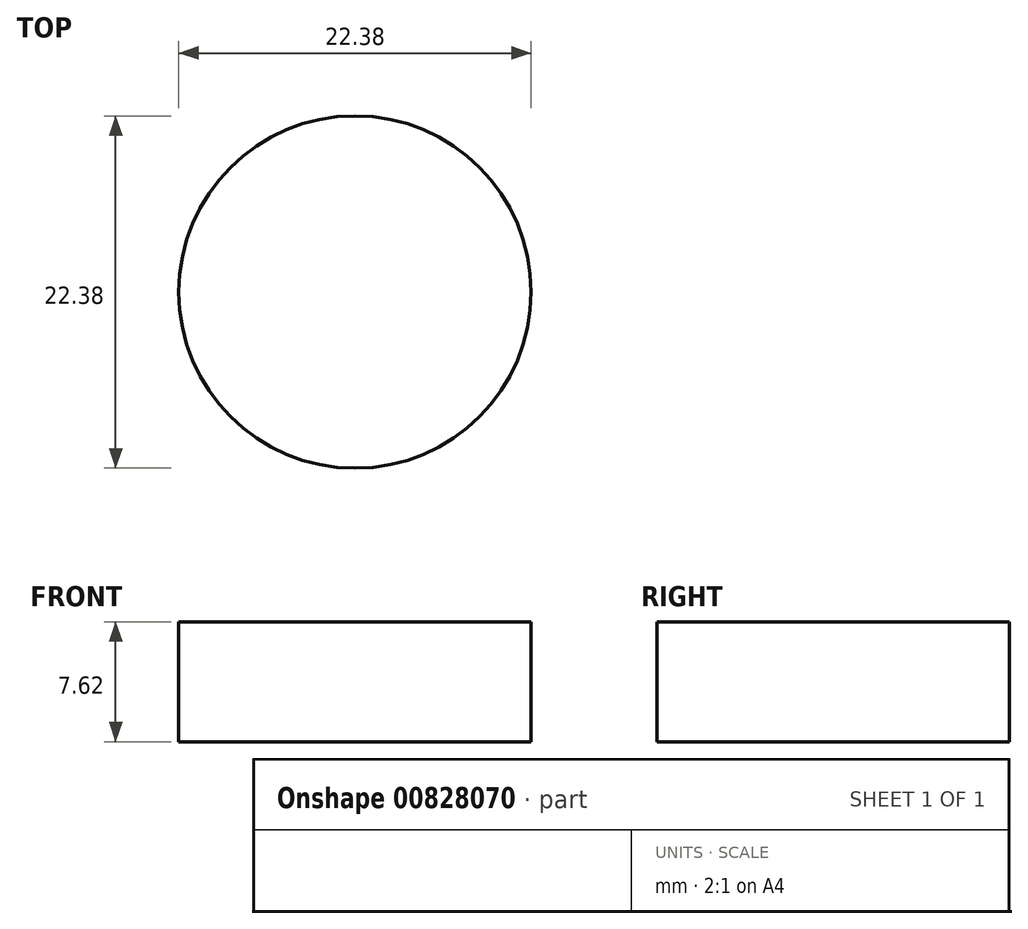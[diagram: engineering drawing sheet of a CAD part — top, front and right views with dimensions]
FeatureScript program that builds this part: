
annotation { "Feature Type Name" : "Feature", "Feature Type Description" : "" }
export const myFeature = defineFeature(function(context is Context, id is Id, definition is map)
    precondition{}
    {
        {
            var Q0;
            Q0=qCreatedBy(makeId("Top.planeOp"),FACE);
            var sketch = newSketch(context, id + "F0", { "sketchPlane" : qUnion([Q0])});
            skCircle(sketch, "E0", {"center": v(0, 0) * mm, "radius": 11.19 * mm});
            skSolve(sketch);
        }
        {
            var Q0;
            Q0=qCreatedBy(makeId("Top.planeOp"),FACE);
            var sketch = newSketch(context, id + "F1", { "sketchPlane" : qUnion([Q0])});
            skLineSegment(sketch, "E1", {"start": v(0, 18) * mm, "end": v(-20.67, -6.89) * mm});
            skLineSegment(sketch, "E2", {"start": v(-20.67, -6.89) * mm, "end": v(12.93, -14.87) * mm});
            skLineSegment(sketch, "E3", {"start": v(12.93, -14.87) * mm, "end": v(9.3, 22.12) * mm});
            skSolve(sketch);
        }
        {
            var Q0;
            Q0=qCreatedBy(makeId("Top.planeOp"),FACE);
            var sketch = newSketch(context, id + "F2", { "sketchPlane" : qUnion([Q0])});
            skLineSegment(sketch, "E4", {"start": v(0, 17.04) * mm, "end": v(8.58, 21.63) * mm});
            skLineSegment(sketch, "E5", {"start": v(8.58, 21.63) * mm, "end": v(0, 17.04) * mm});
            skLineSegment(sketch, "E6", {"start": v(-20.43, -6.65) * mm, "end": v(-54.02, 2.78) * mm});
            skLineSegment(sketch, "E7", {"start": v(-54.02, 2.78) * mm, "end": v(-20.43, -6.65) * mm});
            skLineSegment(sketch, "E8", {"start": v(13.17, -15.1) * mm, "end": v(42.18, -23.33) * mm});
            skLineSegment(sketch, "E9", {"start": v(42.18, -23.33) * mm, "end": v(11.16, -14.54) * mm});
            skLineSegment(sketch, "E10", {"start": v(11.16, -14.54) * mm, "end": v(13.17, -15.1) * mm});
            skLineSegment(sketch, "E11", {"start": v(-20.43, -6.65) * mm, "end": v(-35.65, -41.21) * mm});
            skLineSegment(sketch, "E12", {"start": v(-35.65, -41.21) * mm, "end": v(-20.43, -6.65) * mm});
            skLineSegment(sketch, "E13", {"start": v(13.17, -17.04) * mm, "end": v(8.58, -47.5) * mm});
            skLineSegment(sketch, "E14", {"start": v(8.58, -47.5) * mm, "end": v(13.17, -15.1) * mm});
            skLineSegment(sketch, "E15", {"start": v(0, 17.04) * mm, "end": v(-33.3, 26.38) * mm});
            skLineSegment(sketch, "E16", {"start": v(-33.3, 26.38) * mm, "end": v(0, 17.04) * mm});
            skLineSegment(sketch, "E17", {"start": v(8.58, 21.63) * mm, "end": v(39.28, 28.16) * mm});
            skLineSegment(sketch, "E18", {"start": v(39.28, 28.16) * mm, "end": v(8.58, 21.63) * mm});
            skLineSegment(sketch, "E19", {"start": v(8.58, 21.63) * mm, "end": v(4.04, 43) * mm});
            skLineSegment(sketch, "E20", {"start": v(4.04, 43) * mm, "end": v(8.58, 21.63) * mm});
            skLineSegment(sketch, "E21", {"start": v(0, 17.04) * mm, "end": v(-5.02, 40.66) * mm});
            skLineSegment(sketch, "E22", {"start": v(-5.02, 40.66) * mm, "end": v(0, 17.04) * mm});
            skSolve(sketch);
        }
        {
            var Q0;
            Q0 = qSketchRegion(id + "F0", true);
            var Q1;
            Q1 = qSketchRegion(id + "F1", true);
            var Q2;
            Q2 = qSketchRegion(id + "F2", true);
            extrude(context, id + "F3", {"entities" : qUnion([Q0, Q1, Q2]), "depth" : 7.62 * mm, "offsetDistance" : 25.4 * mm});
        }
    });
